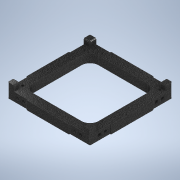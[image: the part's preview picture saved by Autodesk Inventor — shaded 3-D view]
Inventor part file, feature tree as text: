
AUTODESK INVENTOR PART (.ipt)
format: ipt  version: 2022 (Build 260153000, 153)  size: 411,648 bytes
history: native  units: mm
features: extrude x9, sketch x8, projected_geometry x4, fillet x2, chamfer x1
ambient origin geometry x8: Origin, YZ Plane, XZ Plane, XY Plane, X Axis, Y Axis, Z Axis, Center Point
bodies: Solid1 (feature_tree)
feature tree (24):
  extrude  "Extrusion1"  Depth=73.66mm
  extrude  "Extrusion2"  Depth=2.54mm
  extrude  "Extrusion3"  Depth=2.9mm
  fillet  "Fillet1"  Radius=100.0mm
  extrude  "Extrusion4"  Depth=10.0mm TaperAngle=0.0deg
  chamfer  "Chamfer1"  Distance=6.2mm
  extrude  "Extrusion5"  Depth=6.5mm
  fillet  "Fillet2"  Radius=1.2mm
  extrude  "Extrusion6"  Depth=6.5mm
  extrude  "Extrusion7"  Depth=6.5mm
  extrude  "Extrusion8"  TaperAngle=0.0deg  [1 undecoded]
  extrude  "Extrusion9"  Depth=6.5mm TaperAngle=360.0deg
  sketch  "Sketch1"  dims[d0=73.66mm d1=80.01mm]
  sketch  "Sketch4"  dims[d2=85.730001mm d3=2.54mm]
  projected_geometry  "Projected Loop2"
  sketch  "Sketch5"  dims[d4=3.81mm d6=2.9mm d7=100.0mm]
  projected_geometry  "Projected Loop3"
  sketch  "Sketch6"  dims[d8=100.0mm d10=10.0mm d11=0.0mm]
  projected_geometry  "Projected Loop4"
  sketch  "Sketch7"  dims[d13=4.5mm]
  projected_geometry  "Projected Loop5"
  sketch  "Sketch8"  dims[d14=4.5mm]
  sketch  "Sketch10"  dims[d15=4.5mm]
  sketch  "Sketch11"  dims[d16=4.5mm d17=6.2mm d18=0.0mm d19=1.2mm d20=1.2mm d21=25.0mm d22=25.0mm d23=0.0mm d24=0.0mm d25=40.0mm d27=360.0deg d29=1.0mm d30=7.3mm d31=7.3mm d32=6.5mm d33=0.0mm d34=1.0mm d35=2.0mm d36=45.0deg d37=40.0mm d39=360.0deg d50=11.0mm d51=11.0mm d52=11.0mm d53=11.0mm d54=10.0mm d55=0.0mm d56=10.0mm d57=30.5mm d58=30.5mm d59=4.2mm d60=4.2mm d61=7.7mm d62=0.0mm d63=4.2mm d64=4.2mm d67=6.5mm d68=0.0mm d69=4.2mm d70=7.7mm d71=0.0mm d72=6.5mm d73=0.0mm d75=5.0mm d76=5.0mm d77=5.0mm d78=19.5mm d79=19.5mm d80=4.2mm d81=19.5mm d82=7.0mm d83=4.2mm d84=7.0mm d85=4.2mm d86=4.2mm d87=7.0mm d88=7.0mm d89=4.2mm d90=7.0mm d91=4.2mm d92=4.2mm d93=7.0mm d94=19.5mm]
note: 1 required parameter value undecoded (feature->parameter linkage not recoverable at this tier; creation-order binding heuristic only, values carry confidence <= 0.55)
